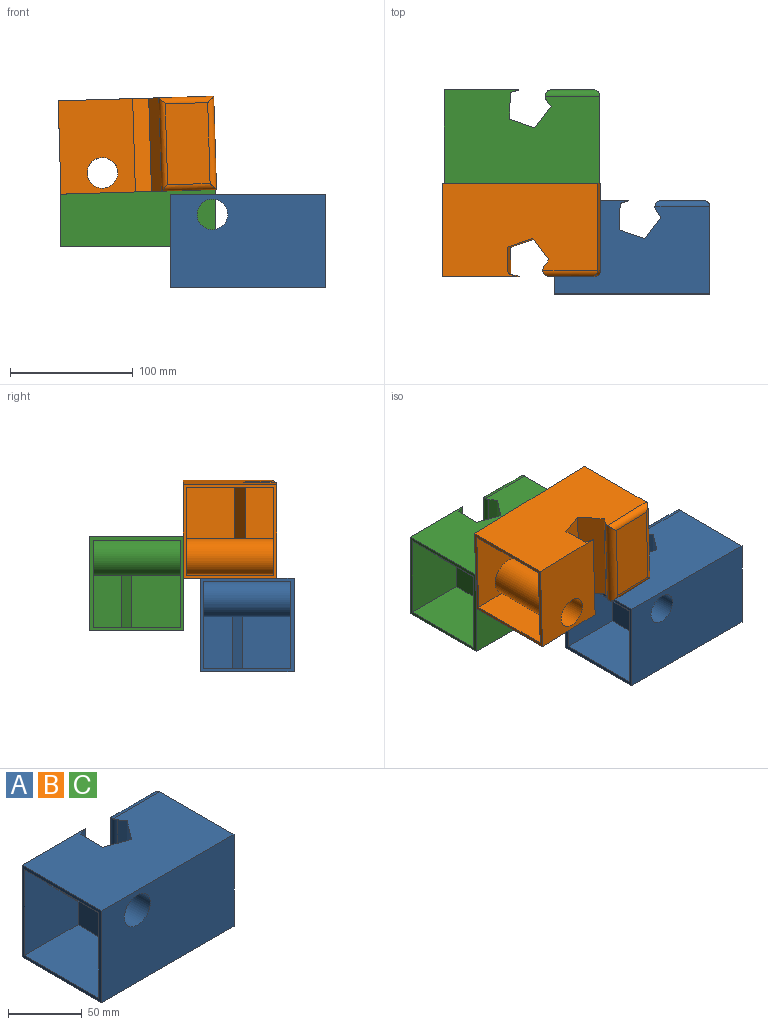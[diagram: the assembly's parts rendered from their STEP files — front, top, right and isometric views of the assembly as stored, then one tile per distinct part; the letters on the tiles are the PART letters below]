
ASSEMBLY  parts=3 mates=1
PART A: 33 faces, bbox 127x76.2x76.2 mm
  f0: plane 76.2x76.2mm, normal (-1,0,0), area 748.4mm2, adj f1,f2,f3,f6,f17,f18,f19,f23
  f1: plane 76.2x60.8mm, normal (0,1,0), area 4142mm2, adj f0,f2,f3,f4,f10
  f2: plane 127x76.2mm, normal (0,0,-1), area 8652.9mm2, adj f0,f1,f5,f6,f8,f9,f10,f11
  f3: plane 127x76.2mm, normal (0,0,1), area 8652.9mm2, adj f0,f1,f5,f6,f8,f9,f10,f11
  f4: cylinder r=12.5mm len=76.2mm, axis (0,1,0), area 5983.4mm2, adj f1,f6
  f5: plane 76.2x71.12mm, normal (1,0,0), area 5419.3mm2, adj f2,f3,f6,f15
  f6: plane 127x76.2mm, normal (0,-1,0), area 9186.7mm2, adj f0,f2,f3,f4,f5
  f7: plane 66.04x34.65mm, normal (0,1,0), area 2288.5mm2, adj f13,f14,f15,f16
  f8: plane 76.2x17.37mm, normal (-0.8,0.6,0), area 1659.6mm2, adj f2,f3,f9,f12
  f9: plane 76.2x5.68mm, normal (-0.82,-0.57,0), area 527.7mm2, adj f2,f3,f8,f14
  f10: plane 76.2x7.04mm, normal (0.29,-0.96,0), area 560.3mm2, adj f1,f2,f3,f11
  f11: plane 76.2x21.78mm, normal (1,-0.02,0), area 1659.6mm2, adj f2,f3,f10,f12
  f12: plane 76.2x20.58mm, normal (0.33,0.94,0), area 1659.6mm2, adj f2,f3,f8,f11
  f13: cylinder r=5.08mm len=44.81mm, axis (1,0,0), area 328.1mm2, adj f2,f7,f14,f15
  f14: cylinder r=5.08mm len=76.2mm, axis (0,0,1), area 814.4mm2, adj f2,f3,f7,f9,f13,f16
  f15: cylinder r=5.08mm len=76.2mm, axis (0,0,1), area 578.6mm2, adj f5,f7,f13,f16
  f16: cylinder r=5.08mm len=44.81mm, axis (-1,0,0), area 328.1mm2, adj f3,f7,f14,f15
  f17: plane 71.12x28.39mm, normal (0,0,-1), area 2019.2mm2, adj f0,f18,f21,f23
  f18: plane 71.12x51.21mm, normal (0,-1,0), area 2942.1mm2, adj f0,f17,f19,f20,f21,f27
  f19: plane 124.46x71.12mm, normal (0,0,1), area 7809.6mm2, adj f0,f18,f22,f23,f25,f26,f27,f28
  f20: plane 84.03x71.12mm, normal (0,0,-1), area 4934.1mm2, adj f18,f21,f22,f23,f25,f26,f27,f28
  f21: cylinder r=15.04mm len=71.12mm, axis (0,1,0), area 5838.5mm2, adj f17,f18,f20,f23
  f22: plane 71.12x68.58mm, normal (-1,0,0), area 4877.4mm2, adj f19,f20,f23,f31
  f23: plane 124.46x71.12mm, normal (0,1,0), area 8151.4mm2, adj f0,f17,f19,f20,f21,f22
  f24: plane 66.04x34.65mm, normal (0,-1,0), area 2288.5mm2, adj f29,f30,f31,f32
  f25: plane 71.12x20.32mm, normal (0.8,-0.6,0), area 1811.5mm2, adj f19,f20,f26,f28
  f26: plane 71.12x7.19mm, normal (0.82,0.57,0), area 623.8mm2, adj f19,f20,f25,f30
  f27: plane 71.12x23.17mm, normal (-1,0.02,0), area 1648.2mm2, adj f18,f19,f20,f28
  f28: plane 71.12x24.07mm, normal (-0.33,-0.94,0), area 1811.5mm2, adj f19,f20,f25,f27
  f29: cylinder r=2.54mm len=39.73mm, axis (1,0,0), area 151.2mm2, adj f19,f24,f30,f31
  f30: cylinder r=2.54mm len=71.12mm, axis (0,0,1), area 386.4mm2, adj f19,f20,f24,f26,f29,f32
  f31: cylinder r=2.54mm len=71.12mm, axis (0,0,1), area 276.4mm2, adj f22,f24,f29,f32
  f32: cylinder r=2.54mm len=39.73mm, axis (-1,0,0), area 151.2mm2, adj f20,f24,f30,f31
PART B: same geometry as A
PART C: same geometry as A
PLACE A t=(39.47,-151.04,-16.15)mm
PLACE B rot(axis=(1,0,0.01),180deg) t=(-49.7,-213.1,-15.93)mm
PLACE C t=(-50.2,-60.7,17.73)mm fixed
MATE revolute B.f4 <-> C.f4  axis (0,1,0) through (-15.78,-136.9,1.41)mm
